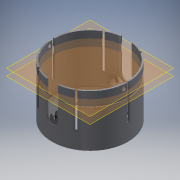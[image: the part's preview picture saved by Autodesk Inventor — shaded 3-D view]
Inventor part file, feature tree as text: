
AUTODESK INVENTOR PART (.ipt)
format: ipt  version: 2016 (Build 200138000, 138)  size: 471,552 bytes
history: native  units: mm
features: sketch x14, extrude x13, reference x8, plane x4, other x2, thicken_offset x2, mirror x1, pattern_circular x1, hole x1
ambient origin geometry x8: Origin, YZ Plane, XZ Plane, XY Plane, X Axis, Y Axis, Z Axis, Center Point
bodies: Solid1 (feature_tree)
feature tree (46):
  extrude  "Extrusion1"  Depth=4.0mm TaperAngle=0.0deg
  extrude  "Extrusion2"  Depth=4.0mm TaperAngle=0.0deg
  sketch  "Sketch3"  dims[d8=4.0mm d9=0.0mm d10=0.0mm d11=0.0mm]
  other  "Work Point1"
  extrude  "Extrusion3"  TaperAngle=0.0deg  [1 undecoded]
  extrude  "Extrusion4"  Depth=0.2mm
  extrude  "Extrusion5"  Depth=2.0mm
  plane  "Work Plane1"
  extrude  "Extrusion6"  Depth=1.0mm
  thicken_offset  "Thicken2"
  thicken_offset  "Thicken3"
  mirror  "Mirror1"
  extrude  "Extrusion7"  [1 undecoded]
  plane  "Work Plane2"
  extrude  "Extrusion8"  Depth=0.523599mm
  sketch  "Sketch9"  dims[d29=50.0mm d30=0.0mm d31=60.0mm d32=360.0deg]
  plane  "Work Plane3"
  plane  "Work Plane4"
  extrude  "Extrusion9"  Depth=60.0mm TaperAngle=360.0deg
  extrude  "Extrusion10"  Depth=50.0mm TaperAngle=0.0deg
  pattern_circular  "Circular Pattern1"  [2 undecoded]
  extrude  "Extrusion11"  Depth=3.0mm
  extrude  "Extrusion12"  Depth=3.0mm
  extrude  "Extrusion13"  Depth=3.0mm
  hole  "Hole1"  [1 undecoded]
  sketch  "Sketch1"  dims[d0=4.0mm d1=0.0mm d2=4.0mm d3=0.0mm]
  reference  "Reference1"
  reference  "Reference2"
  sketch  "Sketch2"  dims[d4=4.0mm d5=0.0mm d6=4.0mm d7=0.0mm]
  reference  "Reference3"
  reference  "Reference4"
  sketch  "Sketch4"  dims[d14=0.2mm d15=0.2mm d16=0.2mm d17=0.2mm]
  sketch  "Sketch5"  dims[d18=4.0mm d19=0.0mm d20=2.0mm]
  reference  "Reference6"
  sketch  "Sketch6"  dims[d21=70.0mm d22=0.0mm d23=1.0mm]
  reference  "Reference7"
  other  "Work Point2"
  sketch  "Sketch7"  dims[d24=-10.0mm d25=-20.0mm]
  sketch  "Sketch8"  dims[d26=70.0mm d27=0.0mm d28=0.523599mm]
  sketch  "Sketch10"  dims[d34=50.0mm d35=0.0mm d36=50.0mm d37=0.0mm]
  sketch  "Sketch11"  dims[d38=3.5mm]
  reference  "Reference8"
  sketch  "Sketch12"  dims[d39=0.0mm d40=0.0mm]
  reference  "Reference9"
  sketch  "Sketch13"  dims[d41=3.0mm]
  sketch  "Sketch14"  dims[d42=3.0mm d43=3.0mm d44=3.0mm d45=3.0mm d46=3.0mm d47=3.0mm d48=3.0mm d49=3.1mm d50=6.0mm d51=4.0mm d52=2.0mm d53=90.0deg d54=6.0mm d55=20.594885mm]
note: 5 required parameter values undecoded (feature->parameter linkage not recoverable at this tier; creation-order binding heuristic only, values carry confidence <= 0.55)
